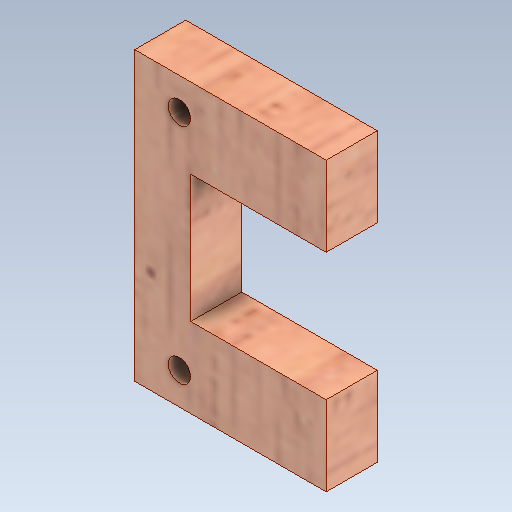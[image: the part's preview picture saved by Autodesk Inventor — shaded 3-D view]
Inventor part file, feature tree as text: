
AUTODESK INVENTOR PART (.ipt)
format: ipt  version: 2020 (Build 240168000, 168)  size: 215,040 bytes
history: native  units: mm
features: other x4, extrude x3, sketch x3, reference x1
ambient origin geometry x8: Origin, YZ Plane, XZ Plane, XY Plane, X Axis, Y Axis, Z Axis, Center Point
bodies: Solid1 (feature_tree)
feature tree (11):
  extrude  "Extrusion1"  Depth=45.0mm
  extrude  "Extrusion3"  TaperAngle=0.0deg  [1 undecoded]
  extrude  "Extrusion4"  Depth=10.0mm TaperAngle=0.0deg
  sketch  "Sketch1"  dims[d0=30.0mm d1=45.0mm]
  sketch  "Sketch3"  dims[d2=8.0mm d3=0.0mm d8=0.0mm]
  reference  "Reference1"
  sketch  "Sketch4"  dims[d9=20.0mm d10=10.0mm d11=0.0mm d15=0.0mm d16=0.0mm d17=3.5mm d18=3.5mm d19=5.0mm d20=7.0mm d21=5.0mm d22=35.0mm]
  parser-record x1  (decoder bookkeeping rows leaked as tree rows — omitted from the tree; the rows remain in map.json)
  other  "0005-00-00 Ansamblu_General.iam"
  other  "Plunger Assembly_Défaut:1"
  other  "plunger_Défaut_4"
note: 1 required parameter value undecoded (feature->parameter linkage not recoverable at this tier; creation-order binding heuristic only, values carry confidence <= 0.55)
note: 1 file-system path scrubbed to <path> (originals preserved in map.json)
